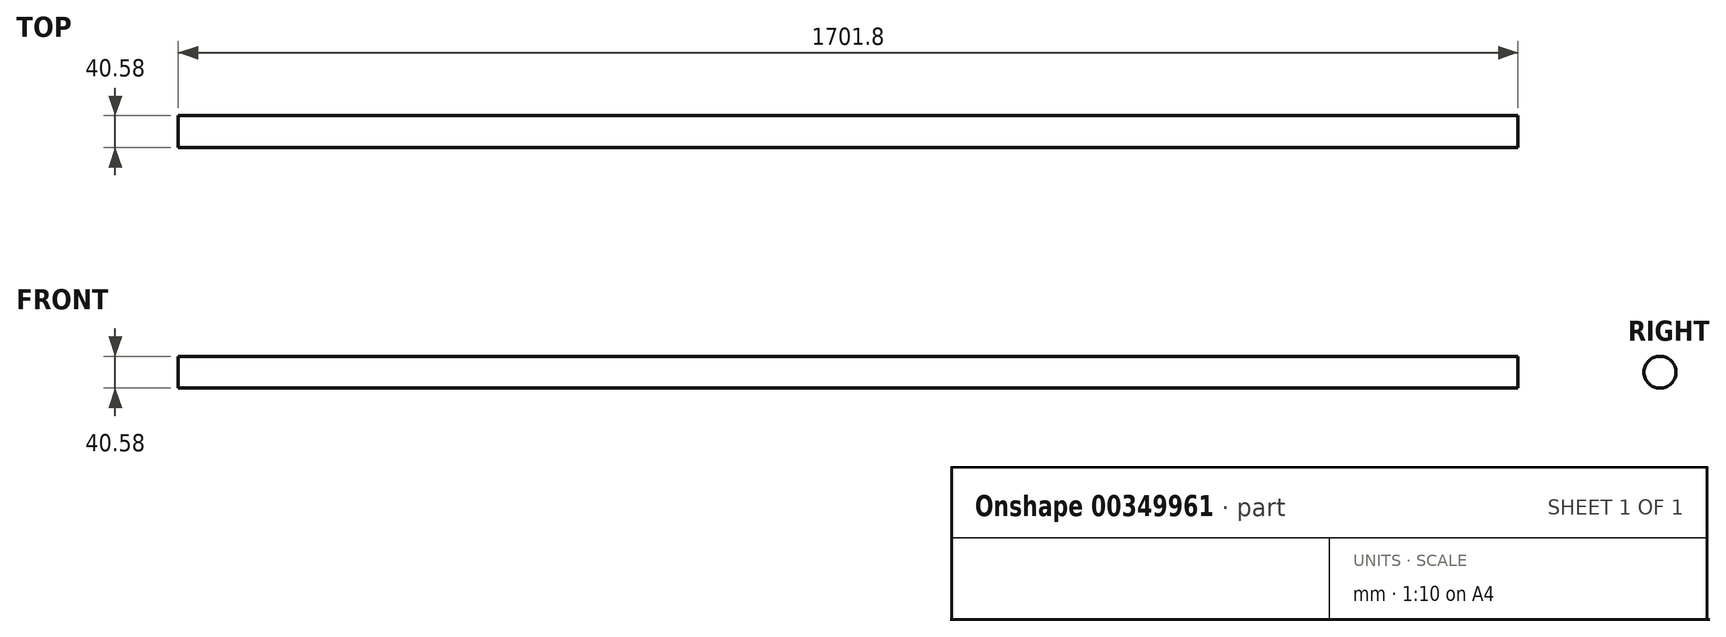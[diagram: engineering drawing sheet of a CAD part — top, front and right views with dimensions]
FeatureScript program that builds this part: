
annotation { "Feature Type Name" : "Feature", "Feature Type Description" : "" }
export const myFeature = defineFeature(function(context is Context, id is Id, definition is map)
    precondition{}
    {
        {
            var Q0;
            Q0=qCreatedBy(makeId("Right.planeOp"),FACE);
            var sketch = newSketch(context, id + "F0", { "sketchPlane" : qUnion([Q0])});
            skCircle(sketch, "E0", {"center": v(0, 0) * mm, "radius": 20.29 * mm});
            skSolve(sketch);
        }
        {
            var Q0;
            Q0 = qSketchRegion(id + "F0", true);
            extrude(context, id + "F1", {"entities" : qUnion([Q0]), "depth" : 1701.8 * mm});
        }
    });
